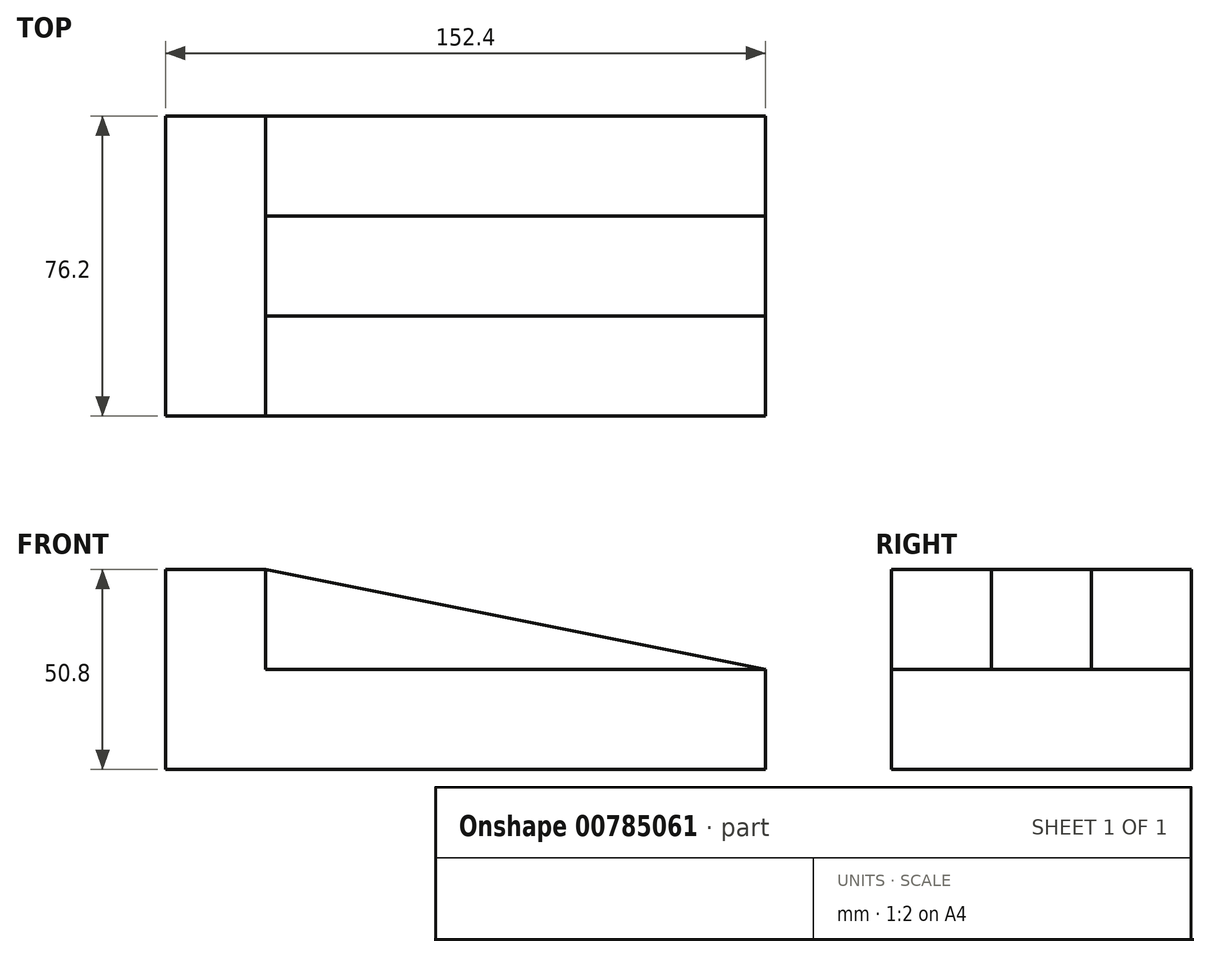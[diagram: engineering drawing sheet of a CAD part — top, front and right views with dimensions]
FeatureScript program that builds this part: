
annotation { "Feature Type Name" : "Feature", "Feature Type Description" : "" }
export const myFeature = defineFeature(function(context is Context, id is Id, definition is map)
    precondition{}
    {
        {
            var Q0;
            Q0=qCreatedBy(makeId("Front.planeOp"),FACE);
            var sketch = newSketch(context, id + "F0", { "sketchPlane" : qUnion([Q0])});
            skLineSegment(sketch, "E0", {"start": v(0, 0) * mm, "end": v(152.4, 0) * mm});
            skLineSegment(sketch, "E1", {"start": v(152.4, 0) * mm, "end": v(152.4, 50.8) * mm});
            skLineSegment(sketch, "E2", {"start": v(152.4, 50.8) * mm, "end": v(0, 50.8) * mm});
            skLineSegment(sketch, "E3", {"start": v(0, 50.8) * mm, "end": v(0, 0) * mm});
            skSolve(sketch);
        }
        {
            var Q0;
            Q0=makeQuery(id+"F0.imprint","IMPRINT",FACE,{"disambiguationData":[TD([[makeQuery(id+"F0.imprint","IMPRINT",EDGE,{"derivedFrom":sQuery(id+"F0.wireOp",EDGE,"E0")}),1.0]])]});
            extrude(context, id + "F1", {"entities" : qUnion([Q0]), "depth" : 76.2 * mm, "offsetDistance" : 25.4 * mm});
        }
        {
            var Q0;
            Q0=makeQuery(id+"F1.opExtrude","CAP_FACE",FACE,{"disambiguationData":[OSD([sQuery(id+"F0.wireOp",EDGE,"E0"),sQuery(id+"F0.wireOp",EDGE,"E1"),sQuery(id+"F0.wireOp",EDGE,"E2"),sQuery(id+"F0.wireOp",EDGE,"E3")])],"isStart":false});
            var sketch = newSketch(context, id + "F2", { "sketchPlane" : qUnion([Q0])});
            skLineSegment(sketch, "E4", {"start": v(152.4, 0) * mm, "end": v(152.4, 25.4) * mm});
            skLineSegment(sketch, "E5", {"start": v(152.4, 25.4) * mm, "end": v(25.4, 25.4) * mm});
            skLineSegment(sketch, "E6", {"start": v(25.4, 25.4) * mm, "end": v(25.4, 50.8) * mm});
            skSolve(sketch);
        }
        {
            var Q0;
            {var subQ0=sQuery(id+"F2.wireOp",EDGE,"E5");Q0=makeQuery(id+"F2.imprint","IMPRINT",FACE,{"disambiguationData":[TD([[makeQuery(id+"F2.imprint","IMPRINT",EDGE,{"derivedFrom":subQ0}),-1.0]])]});}
            extrude(context, id + "F3", {"entities" : qUnion([Q0]), "operationType" : NewBodyOperationType.REMOVE, "oppositeDirection" : true, "depth" : 25.4 * mm, "offsetDistance" : 25.4 * mm});
        }
        {
            var Q0;
            Q0=makeQuery(id+"F1.opExtrude","CAP_FACE",FACE,{"disambiguationData":[OSD([sQuery(id+"F0.wireOp",EDGE,"E0"),sQuery(id+"F0.wireOp",EDGE,"E1"),sQuery(id+"F0.wireOp",EDGE,"E2"),sQuery(id+"F0.wireOp",EDGE,"E3")])],"isStart":true});
            var sketch = newSketch(context, id + "F4", { "sketchPlane" : qUnion([Q0])});
            skLineSegment(sketch, "E7", {"start": v(-152.4, 0) * mm, "end": v(-152.4, 25.4) * mm});
            skLineSegment(sketch, "E8", {"start": v(-152.4, 25.4) * mm, "end": v(-25.4, 25.4) * mm});
            skLineSegment(sketch, "E9", {"start": v(-25.4, 25.4) * mm, "end": v(-25.4, 0) * mm});
            skLineSegment(sketch, "E10", {"start": v(-25.4, 25.4) * mm, "end": v(-25.4, 50.8) * mm});
            skSolve(sketch);
        }
        {
            var Q0;
            {var subQ0=sQuery(id+"F4.wireOp",EDGE,"E8");Q0=makeQuery(id+"F4.imprint","IMPRINT",FACE,{"disambiguationData":[TD([[makeQuery(id+"F4.imprint","IMPRINT",EDGE,{"derivedFrom":subQ0}),1.0]])]});}
            extrude(context, id + "F5", {"entities" : qUnion([Q0]), "operationType" : NewBodyOperationType.REMOVE, "oppositeDirection" : true, "depth" : 25.4 * mm, "offsetDistance" : 25.4 * mm});
        }
        {
            var Q0;
            Q0=makeQuery(id+"F3.boolean.opBoolean","COPY",FACE,{"derivedFrom":makeQuery(id+"F3.opExtrude","CAP_FACE",FACE,{"disambiguationData":[OSD([sQuery(id+"F0.wireOp",EDGE,"E1"),sQuery(id+"F0.wireOp",EDGE,"E2"),sQuery(id+"F2.wireOp",EDGE,"E5"),sQuery(id+"F2.wireOp",EDGE,"E6")])],"isStart":false})});
            var sketch = newSketch(context, id + "F6", { "sketchPlane" : qUnion([Q0])});
            skLineSegment(sketch, "E11", {"start": v(152.4, 25.4) * mm, "end": v(25.4, 50.8) * mm});
            skSolve(sketch);
        }
        {
            var Q0;
            Q0=makeQuery(id+"F6.imprint","IMPRINT",FACE,{"disambiguationData":[TD([[makeQuery(id+"F6.imprint","IMPRINT",EDGE,{"derivedFrom":sQuery(id+"F6.wireOp",EDGE,"E11")}),-1.0]])]});
            extrude(context, id + "F7", {"entities" : qUnion([Q0]), "operationType" : NewBodyOperationType.REMOVE, "oppositeDirection" : true, "depth" : 25.4 * mm, "offsetDistance" : 25.4 * mm});
        }
    });
